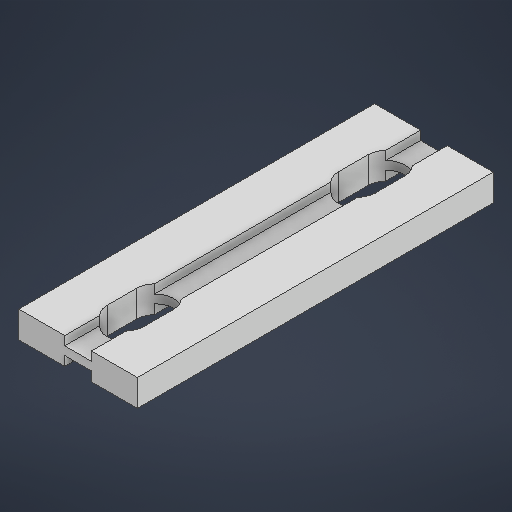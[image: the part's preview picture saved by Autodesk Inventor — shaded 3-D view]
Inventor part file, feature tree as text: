
AUTODESK INVENTOR PART (.ipt)
format: ipt  version: 2025 (Build 290162000, 162)  size: 231,936 bytes
history: native  units: in
note: dims shown in document units (in); Inventor stores cm internally (conversion verified against a paired STEP export)
features: extrude x2, sketch x2
ambient origin geometry x8: Origin, YZ Plane, XZ Plane, XY Plane, X Axis, Y Axis, Z Axis, Center Point
bodies: Solid1 (feature_tree)
feature tree (4):
  extrude  "Extrusion1"  Depth=0.1772in
  extrude  "Extrusion2"  Depth=0.1181in
  sketch  "Sketch1"  dims[d0=0.7874in d1=0.1772in]
  sketch  "Sketch2"  dims[d2=0.1772in d3=0.1181in d4=2.3622in d5=0.0in d6=0.2441in d7=0.1969in d8=0.315in d9=2.3622in d10=0.0in]
